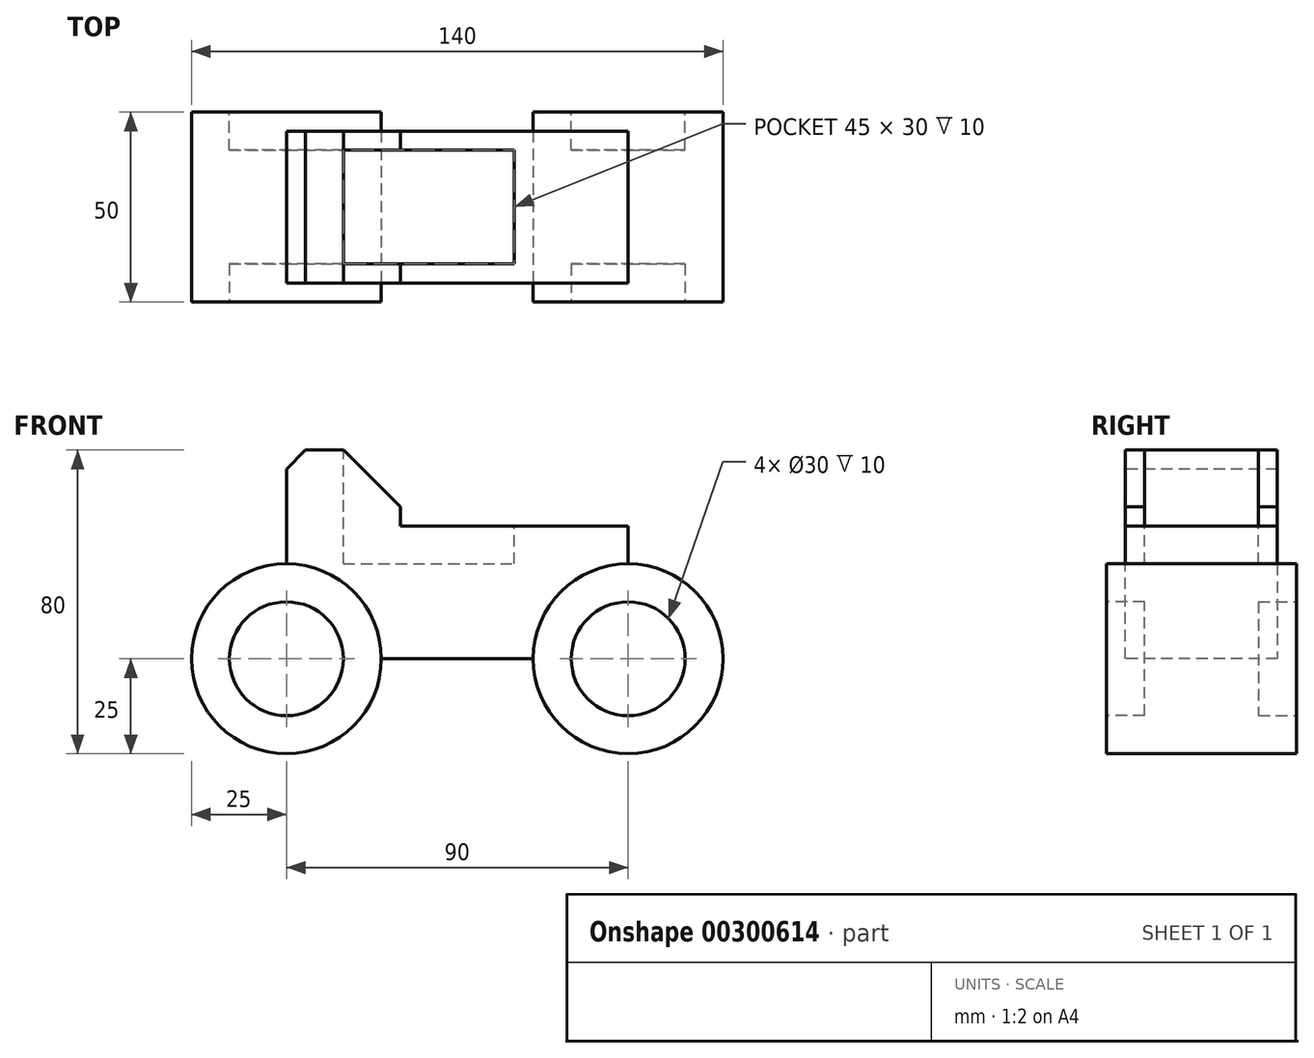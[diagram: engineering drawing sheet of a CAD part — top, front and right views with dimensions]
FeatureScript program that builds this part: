
annotation { "Feature Type Name" : "Feature", "Feature Type Description" : "" }
export const myFeature = defineFeature(function(context is Context, id is Id, definition is map)
    precondition{}
    {
        {
            var Q0;
            Q0=qCreatedBy(makeId("Front.planeOp"),FACE);
            var sketch = newSketch(context, id + "F0", { "sketchPlane" : qUnion([Q0])});
            skLineSegment(sketch, "E0.bottom", {"start": v(45, 27.5) * mm, "end": v(-45, 27.5) * mm});
            skLineSegment(sketch, "E0.top", {"start": v(45, -27.5) * mm, "end": v(-45, -27.5) * mm});
            skLineSegment(sketch, "E0.left", {"start": v(45, 27.5) * mm, "end": v(45, -27.5) * mm});
            skLineSegment(sketch, "E0.right", {"start": v(-45, 27.5) * mm, "end": v(-45, -27.5) * mm});
            skPoint(sketch, "E0.middle", {"position": v(0, 0) * mm});
            skSolve(sketch);
        }
        {
            var Q0;
            Q0 = qSketchRegion(id + "F0", true);
            extrude(context, id + "F1", {"entities" : qUnion([Q0]), "depth" : 40 * mm});
        }
        {
            var Q0;
            Q0=makeQuery(id+"F1.opExtrude","CAP_FACE",FACE,{"disambiguationData":[OSD([sQuery(id+"F0.wireOp",EDGE,"E0.bottom"),sQuery(id+"F0.wireOp",EDGE,"E0.top"),sQuery(id+"F0.wireOp",EDGE,"E0.left"),sQuery(id+"F0.wireOp",EDGE,"E0.right")])],"isStart":false});
            var sketch = newSketch(context, id + "F2", { "sketchPlane" : qUnion([Q0])});
            skCircle(sketch, "E1", {"center": v(-45, -27.5) * mm, "radius": 25 * mm});
            skCircle(sketch, "E2", {"center": v(45, -27.5) * mm, "radius": 25 * mm});
            skSolve(sketch);
        }
        {
            var Q0;
            Q0 = qSketchRegion(id + "F2", true);
            extrude(context, id + "F3", {"entities" : qUnion([Q0]), "operationType" : NewBodyOperationType.ADD, "oppositeDirection" : true, "depth" : 45 * mm});
        }
        {
            var Q0;
            Q0=makeQuery(id+"F3.boolean.opBoolean","MERGE",FACE,{"derivedFrom":[makeQuery(id+"F1.opExtrude","CAP_FACE",FACE,{"disambiguationData":[OSD([sQuery(id+"F0.wireOp",EDGE,"E0.bottom"),sQuery(id+"F0.wireOp",EDGE,"E0.top"),sQuery(id+"F0.wireOp",EDGE,"E0.left"),sQuery(id+"F0.wireOp",EDGE,"E0.right")])],"isStart":false}),makeQuery(id+"F3.opExtrude","CAP_FACE",FACE,{"disambiguationData":[OSD([sQuery(id+"F2.wireOp",EDGE,"E1")])],"isStart":true}),makeQuery(id+"F3.opExtrude","CAP_FACE",FACE,{"disambiguationData":[OSD([sQuery(id+"F2.wireOp",EDGE,"E2")])],"isStart":true})]});
            var sketch = newSketch(context, id + "F4", { "sketchPlane" : qUnion([Q0])});
            skCircle(sketch, "E3", {"center": v(-45, -27.5) * mm, "radius": 25 * mm});
            skCircle(sketch, "E4", {"center": v(45, -27.5) * mm, "radius": 25 * mm});
            skSolve(sketch);
        }
        {
            var Q0;
            Q0 = qSketchRegion(id + "F4", true);
            extrude(context, id + "F5", {"entities" : qUnion([Q0]), "operationType" : NewBodyOperationType.ADD, "depth" : 5 * mm});
        }
        {
            var Q0;
            Q0=makeQuery(id+"F1.opExtrude","SWEPT_FACE",FACE,{"disambiguationData":[OSD([sQuery(id+"F0.wireOp",EDGE,"E0.bottom")])]});
            var sketch = newSketch(context, id + "F6", { "sketchPlane" : qUnion([Q0])});
            skLineSegment(sketch, "E5.bottom", {"start": v(45, -40) * mm, "end": v(-15, -40) * mm});
            skLineSegment(sketch, "E5.top", {"start": v(45, 0) * mm, "end": v(-15, 0) * mm});
            skLineSegment(sketch, "E5.left", {"start": v(45, -40) * mm, "end": v(45, 0) * mm});
            skLineSegment(sketch, "E5.right", {"start": v(-15, -40) * mm, "end": v(-15, 0) * mm});
            skSolve(sketch);
        }
        {
            var Q0;
            Q0 = qSketchRegion(id + "F6", true);
            extrude(context, id + "F7", {"entities" : qUnion([Q0]), "operationType" : NewBodyOperationType.REMOVE, "oppositeDirection" : true, "depth" : 20 * mm});
        }
        {
            var Q0;
            Q0=makeQuery(id+"F7.boolean.opBoolean","COPY",FACE,{"derivedFrom":makeQuery(id+"F7.opExtrude","CAP_FACE",FACE,{"disambiguationData":[OSD([sQuery(id+"F6.wireOp",EDGE,"E5.bottom"),sQuery(id+"F6.wireOp",EDGE,"E5.top"),sQuery(id+"F6.wireOp",EDGE,"E5.left"),sQuery(id+"F6.wireOp",EDGE,"E5.right")])],"isStart":false})});
            var sketch = newSketch(context, id + "F8", { "sketchPlane" : qUnion([Q0])});
            skLineSegment(sketch, "E6.bottom", {"start": v(-15, -5) * mm, "end": v(15, -5) * mm});
            skLineSegment(sketch, "E6.top", {"start": v(-15, -35) * mm, "end": v(15, -35) * mm});
            skLineSegment(sketch, "E6.left", {"start": v(-15, -5) * mm, "end": v(-15, -35) * mm});
            skLineSegment(sketch, "E6.right", {"start": v(15, -5) * mm, "end": v(15, -35) * mm});
            skSolve(sketch);
        }
        {
            var Q0;
            Q0 = qSketchRegion(id + "F8", true);
            extrude(context, id + "F9", {"entities" : qUnion([Q0]), "operationType" : NewBodyOperationType.REMOVE, "oppositeDirection" : true, "depth" : 10 * mm});
        }
        {
            var Q0;
            Q0=makeQuery(id+"F1.opExtrude","SWEPT_FACE",FACE,{"disambiguationData":[OSD([sQuery(id+"F0.wireOp",EDGE,"E0.bottom")])]});
            var sketch = newSketch(context, id + "F10", { "sketchPlane" : qUnion([Q0])});
            skLineSegment(sketch, "E7.bottom", {"start": v(-30, -5) * mm, "end": v(-15, -5) * mm});
            skLineSegment(sketch, "E7.top", {"start": v(-30, -35) * mm, "end": v(-15, -35) * mm});
            skLineSegment(sketch, "E7.left", {"start": v(-30, -5) * mm, "end": v(-30, -35) * mm});
            skLineSegment(sketch, "E7.right", {"start": v(-15, -5) * mm, "end": v(-15, -35) * mm});
            skSolve(sketch);
        }
        {
            var Q0;
            Q0 = qSketchRegion(id + "F10", true);
            extrude(context, id + "F11", {"entities" : qUnion([Q0]), "operationType" : NewBodyOperationType.REMOVE, "oppositeDirection" : true, "depth" : 30 * mm});
        }
        {
            var Q0;
            Q0=makeQuery(id+"F3.boolean.opBoolean","MERGE",FACE,{"derivedFrom":[makeQuery(id+"F1.opExtrude","CAP_FACE",FACE,{"disambiguationData":[OSD([sQuery(id+"F0.wireOp",EDGE,"E0.bottom"),sQuery(id+"F0.wireOp",EDGE,"E0.top"),sQuery(id+"F0.wireOp",EDGE,"E0.left"),sQuery(id+"F0.wireOp",EDGE,"E0.right")])],"isStart":false}),makeQuery(id+"F3.opExtrude","CAP_FACE",FACE,{"disambiguationData":[OSD([sQuery(id+"F2.wireOp",EDGE,"E1")])],"isStart":true}),makeQuery(id+"F3.opExtrude","CAP_FACE",FACE,{"disambiguationData":[OSD([sQuery(id+"F2.wireOp",EDGE,"E2")])],"isStart":true})]});
            var sketch = newSketch(context, id + "F12", { "sketchPlane" : qUnion([Q0])});
            skLineSegment(sketch, "E8", {"start": v(-30, 27.5) * mm, "end": v(-15, 12.5) * mm});
            skLineSegment(sketch, "E9", {"start": v(-40, 27.5) * mm, "end": v(-45, 22.5) * mm});
            skSolve(sketch);
        }
        {
            var Q0;
            {var subQ0=sQuery(id+"F12.wireOp",EDGE,"E8");Q0=makeQuery(id+"F12.imprint","IMPRINT",FACE,{"disambiguationData":[TD([[makeQuery(id+"F12.imprint","IMPRINT",EDGE,{"derivedFrom":subQ0}),1.0]])]});}
            var Q1;
            {var subQ0=sQuery(id+"F12.wireOp",EDGE,"E9");Q1=makeQuery(id+"F12.imprint","IMPRINT",FACE,{"disambiguationData":[TD([[makeQuery(id+"F12.imprint","IMPRINT",EDGE,{"derivedFrom":subQ0}),-1.0]])]});}
            extrude(context, id + "F13", {"entities" : qUnion([Q0, Q1]), "operationType" : NewBodyOperationType.REMOVE, "endBound" : BoundingType.THROUGH_ALL, "oppositeDirection" : true, "depth" : 25 * mm});
        }
        {
            var Q0;
            Q0=makeQuery(id+"F5.opExtrude","CAP_FACE",FACE,{"disambiguationData":[OSD([sQuery(id+"F4.wireOp",EDGE,"E3")])],"isStart":false});
            var sketch = newSketch(context, id + "F14", { "sketchPlane" : qUnion([Q0])});
            skCircle(sketch, "E10", {"center": v(-45, -27.5) * mm, "radius": 15 * mm});
            skSolve(sketch);
        }
        {
            var Q0;
            Q0 = qSketchRegion(id + "F14", true);
            extrude(context, id + "F15", {"entities" : qUnion([Q0]), "operationType" : NewBodyOperationType.REMOVE, "oppositeDirection" : true, "depth" : 10 * mm});
        }
        {
            var Q0;
            Q0=makeQuery(id+"F5.opExtrude","CAP_FACE",FACE,{"disambiguationData":[OSD([sQuery(id+"F4.wireOp",EDGE,"E4")])],"isStart":false});
            var sketch = newSketch(context, id + "F16", { "sketchPlane" : qUnion([Q0])});
            skCircle(sketch, "E11", {"center": v(45, -27.5) * mm, "radius": 15 * mm});
            skSolve(sketch);
        }
        {
            var Q0;
            Q0 = qSketchRegion(id + "F16", true);
            extrude(context, id + "F17", {"entities" : qUnion([Q0]), "operationType" : NewBodyOperationType.REMOVE, "oppositeDirection" : true, "depth" : 10 * mm});
        }
        {
            var Q0;
            Q0=makeQuery(id+"F3.opExtrude","CAP_FACE",FACE,{"disambiguationData":[OSD([sQuery(id+"F2.wireOp",EDGE,"E2")])],"isStart":false});
            var sketch = newSketch(context, id + "F18", { "sketchPlane" : qUnion([Q0])});
            skCircle(sketch, "E12", {"center": v(-45, -27.5) * mm, "radius": 15 * mm});
            skSolve(sketch);
        }
        {
            var Q0;
            Q0 = qSketchRegion(id + "F18", true);
            extrude(context, id + "F19", {"entities" : qUnion([Q0]), "operationType" : NewBodyOperationType.REMOVE, "oppositeDirection" : true, "depth" : 10 * mm});
        }
        {
            var Q0;
            Q0=makeQuery(id+"F3.opExtrude","CAP_FACE",FACE,{"disambiguationData":[OSD([sQuery(id+"F2.wireOp",EDGE,"E1")])],"isStart":false});
            var sketch = newSketch(context, id + "F20", { "sketchPlane" : qUnion([Q0])});
            skCircle(sketch, "E13", {"center": v(45, -27.5) * mm, "radius": 15 * mm});
            skSolve(sketch);
        }
        {
            var Q0;
            Q0 = qSketchRegion(id + "F20", true);
            extrude(context, id + "F21", {"entities" : qUnion([Q0]), "operationType" : NewBodyOperationType.REMOVE, "oppositeDirection" : true, "depth" : 10 * mm});
        }
    });
